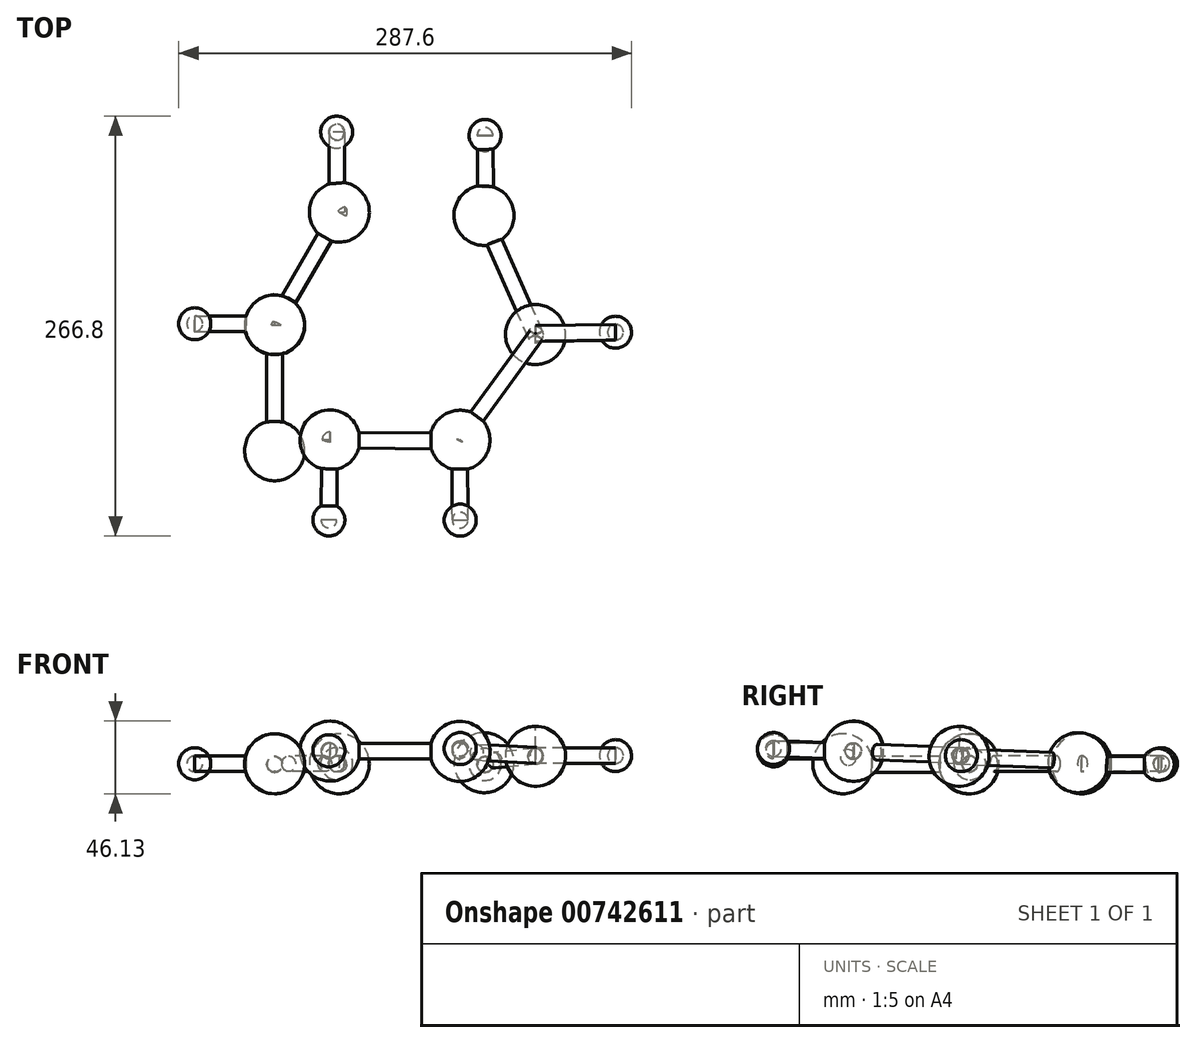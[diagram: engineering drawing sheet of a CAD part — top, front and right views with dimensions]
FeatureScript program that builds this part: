
annotation { "Feature Type Name" : "Feature", "Feature Type Description" : "" }
export const myFeature = defineFeature(function(context is Context, id is Id, definition is map)
    precondition{}
    {
        {
            var Q0;
            Q0=qCreatedBy(makeId("Front.planeOp"),FACE);
            var sketch = newSketch(context, id + "F0", { "sketchPlane" : qUnion([Q0])});
            skLineSegment(sketch, "E0", {"start": v(0, 0) * mm, "end": v(0, 38.1) * mm});
            skArc(sketch, "E1", {"start": v(0, 0) * mm, "mid": v(19.05, 19.05) * mm, "end": v(0, 38.1) * mm});
            skSolve(sketch);
        }
        {
            var Q0;
            {var subQ0=sQuery(id+"F0.wireOp",EDGE,"E0");Q0=makeQuery(id+"F0.imprint","IMPRINT",FACE,{"disambiguationData":[TD([[makeQuery(id+"F0.imprint","IMPRINT",EDGE,{"derivedFrom":subQ0}),-1.0]])]});}
            var Q1;
            Q1=sQuery(id+"F0.wireOp",EDGE,"E0");
            revolve(context, id + "F1", {"surfaceOperationType" : NewSurfaceOperationType.NEW, "entities" : qUnion([Q0]), "axis" : qUnion([Q1]), "revolveType" : RevolveType.FULL});
        }
        {
            var Q0;
            Q0=qCreatedBy(makeId("Front.planeOp"),FACE);
            cPlane(context, id + "F2", {"entities" : qUnion([Q0]), "cplaneType" : CPlaneType.OFFSET, "offset" : 16.5 * mm, "oppositeDirection" : true, "width" : 152.4 * mm, "height" : 152.4 * mm});
        }
        {
            var Q0;
            Q0=qCreatedBy(id+"F2.planeOp",FACE);
            var sketch = newSketch(context, id + "F3", { "sketchPlane" : qUnion([Q0])});
            skPoint(sketch, "E2.middle", {"position": v(0, 18.68) * mm});
            skCircle(sketch, "E3", {"center": v(0, 18.68) * mm, "radius": 4.99 * mm});
            skSolve(sketch);
        }
        {
            var Q0;
            Q0=makeQuery(id+"F3.imprint","IMPRINT",FACE,{"disambiguationData":[TD([[makeQuery(id+"F3.imprint","IMPRINT",EDGE,{"derivedFrom":sQuery(id+"F3.wireOp",EDGE,"E3")}),1.0]])]});
            extrude(context, id + "F4", {"entities" : qUnion([Q0]), "operationType" : NewBodyOperationType.ADD, "oppositeDirection" : true, "depth" : 63.5 * mm, "offsetDistance" : 25.4 * mm});
        }
        {
            var Q0;
            Q0=makeQuery(id+"F4.opExtrude","CAP_FACE",FACE,{"disambiguationData":[OSD([sQuery(id+"F3.wireOp",EDGE,"E3")])],"isStart":false});
            var sketch = newSketch(context, id + "F5", { "sketchPlane" : qUnion([Q0])});
            skArc(sketch, "E4", {"start": v(0, 0) * mm, "mid": v(18.95, 19.05) * mm, "end": v(0, 38.1) * mm});
            skLineSegment(sketch, "E5", {"start": v(0, 38.1) * mm, "end": v(0, 0) * mm});
            skSolve(sketch);
        }
        {
            var Q0;
            {var subQ0=sQuery(id+"F5.wireOp",EDGE,"E4");Q0=makeQuery(id+"F5.imprint","IMPRINT",FACE,{"disambiguationData":[TD([[makeQuery(id+"F5.imprint","IMPRINT",EDGE,{"derivedFrom":subQ0}),1.0]])]});}
            var Q1;
            Q1=sQuery(id+"F5.wireOp",EDGE,"E5");
            revolve(context, id + "F6", {"operationType" : NewBodyOperationType.ADD, "surfaceOperationType" : NewSurfaceOperationType.NEW, "entities" : qUnion([Q0]), "axis" : qUnion([Q1]), "revolveType" : RevolveType.FULL});
        }
        {
            var Q0;
            Q0=sQuery(id+"F5.wireOp",EDGE,"E5");
            var Q1;
            Q1=qCreatedBy(makeId("Right.planeOp"),FACE);
            cPlane(context, id + "F7", {"entities" : qUnion([Q0, Q1]), "cplaneType" : CPlaneType.LINE_ANGLE, "offset" : 25.4 * mm, "angle" : 120 * degree, "width" : 152.4 * mm, "height" : 152.4 * mm});
        }
        {
            var Q0;
            Q0=qCreatedBy(id+"F7.planeOp",FACE);
            var sketch = newSketch(context, id + "F8", { "sketchPlane" : qUnion([Q0])});
            skLineSegment(sketch, "E6", {"start": v(40.25, 0) * mm, "end": v(40.25, 38.1) * mm});
            skLineSegment(sketch, "E7", {"start": v(40.25, 0) * mm, "end": v(40.25, 19.05) * mm});
            skCircle(sketch, "E8", {"center": v(40.25, 19.05) * mm, "radius": 5 * mm});
            skSolve(sketch);
        }
        {
            var Q0;
            {var subQ1=sQuery(id+"F8.wireOp",EDGE,"E6");var subQ3=makeQuery(id+"F8.imprint","IMPRINT",VERTEX,{"derivedFrom":subQ1});var subQ4=makeQuery(id+"F8.imprint","IMPRINT",EDGE,{"disambiguationData":[TD([[subQ3,-1.0]])],"derivedFrom":subQ1});Q0=qUnion([makeQuery(id+"F8.imprint","IMPRINT",FACE,{"disambiguationData":[TD([[subQ4,1.0]])]}),makeQuery(id+"F8.imprint","IMPRINT",FACE,{"disambiguationData":[TD([[subQ4,-1.0]])]})]);}
            extrude(context, id + "F9", {"entities" : qUnion([Q0]), "operationType" : NewBodyOperationType.ADD, "depth" : 82.55 * mm, "offsetDistance" : 25.4 * mm});
        }
        {
            var Q0;
            Q0=makeQuery(id+"F9.opExtrude","CAP_FACE",FACE,{"disambiguationData":[OSD([sQuery(id+"F8.wireOp",EDGE,"E8")])],"isStart":false});
            var sketch = newSketch(context, id + "F10", { "sketchPlane" : qUnion([Q0])});
            skLineSegment(sketch, "E9", {"start": v(40.25, 24.04) * mm, "end": v(40.25, 14.06) * mm});
            skLineSegment(sketch, "E10", {"start": v(40.25, 14.06) * mm, "end": v(40.25, 24.04) * mm});
            skLineSegment(sketch, "E11", {"start": v(40.25, 14.06) * mm, "end": v(40.25, 19.05) * mm});
            skLineSegment(sketch, "E12", {"start": v(40.25, 19.05) * mm, "end": v(40.25, 38.1) * mm});
            skLineSegment(sketch, "E13", {"start": v(40.25, 19.05) * mm, "end": v(40.25, 0) * mm});
            skArc(sketch, "E14", {"start": v(40.25, 0) * mm, "mid": v(59.3, 19.05) * mm, "end": v(40.25, 38.1) * mm});
            skSolve(sketch);
        }
        {
            var Q0;
            {var subQ4=sQuery(id+"F10.wireOp",EDGE,"E13");Q0=makeQuery(id+"F10.imprint","IMPRINT",FACE,{"disambiguationData":[TD([[makeQuery(id+"F10.imprint","IMPRINT",EDGE,{"derivedFrom":subQ4}),1.0]])]});}
            var Q1;
            Q1=sQuery(id+"F10.wireOp",EDGE,"E11");
            revolve(context, id + "F11", {"operationType" : NewBodyOperationType.ADD, "surfaceOperationType" : NewSurfaceOperationType.NEW, "entities" : qUnion([Q0]), "axis" : qUnion([Q1]), "revolveType" : RevolveType.FULL});
        }
        {
            var Q0;
            Q0=qCreatedBy(makeId("Right.planeOp"),FACE);
            cPlane(context, id + "F12", {"entities" : qUnion([Q0]), "cplaneType" : CPlaneType.OFFSET, "offset" : 40.13 * mm, "width" : 152.4 * mm, "height" : 152.4 * mm});
        }
        {
            var Q0;
            Q0=qCreatedBy(id+"F12.planeOp",FACE);
            var sketch = newSketch(context, id + "F13", { "sketchPlane" : qUnion([Q0])});
            skLineSegment(sketch, "E15", {"start": v(137.87, 4.1) * mm, "end": v(163.67, 32.13) * mm});
            skCircle(sketch, "E16", {"center": v(150.77, 18.11) * mm, "radius": 5 * mm});
            skSolve(sketch);
        }
        {
            var Q0;
            Q0=qCreatedBy(id+"F7.planeOp",FACE);
            cPlane(context, id + "F14", {"entities" : qUnion([Q0]), "cplaneType" : CPlaneType.OFFSET, "offset" : 81.53 * mm, "width" : 152.4 * mm, "height" : 152.4 * mm});
        }
        {
            var Q0;
            Q0=sQuery(id+"F13.wireOp",EDGE,"E15");
            var Q1;
            Q1=qCreatedBy(id+"F14.planeOp",FACE);
            cPlane(context, id + "F15", {"entities" : qUnion([Q0, Q1]), "cplaneType" : CPlaneType.LINE_ANGLE, "offset" : 25.4 * mm, "angle" : 120 * degree, "width" : 152.4 * mm, "height" : 152.4 * mm});
        }
        {
            var Q0;
            Q0=sQuery(id+"F13.wireOp",EDGE,"E16");
            extrude(context, id + "F16", {"bodyType" : ToolBodyType.SURFACE, "surfaceEntities" : qUnion([Q0]), "depth" : 82.55 * mm, "offsetDistance" : 25.4 * mm});
        }
        {
            var Q0;
            Q0=qCreatedBy(id+"F15.planeOp",FACE);
            cPlane(context, id + "F17", {"entities" : qUnion([Q0]), "cplaneType" : CPlaneType.OFFSET, "offset" : 92.2 * mm, "width" : 152.4 * mm, "height" : 152.4 * mm});
        }
        {
            var Q0;
            Q0=qCreatedBy(id+"F17.planeOp",FACE);
            var sketch = newSketch(context, id + "F18", { "sketchPlane" : qUnion([Q0])});
            skLineSegment(sketch, "E17", {"start": v(162.64, 11.86) * mm, "end": v(162.64, 1.88) * mm});
            skLineSegment(sketch, "E18", {"start": v(162.64, 1.88) * mm, "end": v(162.64, 6.87) * mm});
            skLineSegment(sketch, "E19", {"start": v(162.64, 6.87) * mm, "end": v(162.64, 25.92) * mm});
            skLineSegment(sketch, "E20", {"start": v(162.64, 6.87) * mm, "end": v(162.64, -12.18) * mm});
            skArc(sketch, "E21", {"start": v(162.64, -12.18) * mm, "mid": v(181.7, 6.87) * mm, "end": v(162.64, 25.92) * mm});
            skSolve(sketch);
        }
        {
            var Q0;
            {var subQ3=sQuery(id+"F18.wireOp",EDGE,"E21");Q0=makeQuery(id+"F18.imprint","IMPRINT",FACE,{"disambiguationData":[TD([[makeQuery(id+"F18.imprint","IMPRINT",EDGE,{"derivedFrom":subQ3}),1.0]])]});}
            var Q1;
            Q1=sQuery(id+"F18.wireOp",EDGE,"E19");
            revolve(context, id + "F19", {"surfaceOperationType" : NewSurfaceOperationType.NEW, "entities" : qUnion([Q0]), "axis" : qUnion([Q1]), "revolveType" : RevolveType.FULL});
        }
        {
            var Q0;
            Q0=sQuery(id+"F18.wireOp",EDGE,"E20");
            var Q1;
            Q1=qCreatedBy(id+"F17.planeOp",FACE);
            cPlane(context, id + "F20", {"entities" : qUnion([Q0, Q1]), "cplaneType" : CPlaneType.LINE_ANGLE, "offset" : 25.4 * mm, "angle" : 120 * degree, "oppositeDirection" : true, "width" : 152.4 * mm, "height" : 152.4 * mm});
        }
        {
            var Q0;
            Q0=qCreatedBy(id+"F20.planeOp",FACE);
            var sketch = newSketch(context, id + "F21", { "sketchPlane" : qUnion([Q0])});
            skLineSegment(sketch, "E22", {"start": v(180.95, 54.99) * mm, "end": v(180.95, -1.08) * mm});
            skLineSegment(sketch, "E23", {"start": v(180.95, -1.08) * mm, "end": v(180.95, 26.96) * mm});
            skCircle(sketch, "E24", {"center": v(180.95, 26.96) * mm, "radius": 5 * mm});
            skSolve(sketch);
        }
        {
            var Q0;
            {var subQ1=sQuery(id+"F21.wireOp",EDGE,"E22");var subQ3=makeQuery(id+"F21.imprint","IMPRINT",VERTEX,{"derivedFrom":subQ1});var subQ4=makeQuery(id+"F21.imprint","IMPRINT",EDGE,{"disambiguationData":[TD([[subQ3,-1.0]])],"derivedFrom":subQ1});Q0=qUnion([makeQuery(id+"F21.imprint","IMPRINT",FACE,{"disambiguationData":[TD([[subQ4,-1.0]])]}),makeQuery(id+"F21.imprint","IMPRINT",FACE,{"disambiguationData":[TD([[subQ4,1.0]])]})]);}
            extrude(context, id + "F22", {"entities" : qUnion([Q0]), "operationType" : NewBodyOperationType.ADD, "depth" : 82.55 * mm, "offsetDistance" : 25.4 * mm});
        }
        {
            var Q0;
            Q0=makeQuery(id+"F22.opExtrude","CAP_FACE",FACE,{"disambiguationData":[OSD([sQuery(id+"F21.wireOp",EDGE,"E24")])],"isStart":false});
            var sketch = newSketch(context, id + "F23", { "sketchPlane" : qUnion([Q0])});
            skLineSegment(sketch, "E25", {"start": v(180.87, 21.97) * mm, "end": v(180.87, 31.95) * mm});
            skLineSegment(sketch, "E26", {"start": v(180.87, 31.95) * mm, "end": v(180.95, 26.96) * mm});
            skLineSegment(sketch, "E27", {"start": v(180.95, 26.96) * mm, "end": v(180.95, 7.9) * mm});
            skLineSegment(sketch, "E28", {"start": v(180.95, 26.96) * mm, "end": v(180.87, 46) * mm});
            skArc(sketch, "E29", {"start": v(180.87, 46) * mm, "mid": v(161.9, 26.91) * mm, "end": v(180.95, 7.9) * mm});
            skSolve(sketch);
        }
        {
            var Q0;
            {var subQ4=sQuery(id+"F23.wireOp",EDGE,"E29");Q0=makeQuery(id+"F23.imprint","IMPRINT",FACE,{"disambiguationData":[TD([[makeQuery(id+"F23.imprint","IMPRINT",EDGE,{"derivedFrom":subQ4}),1.0]])]});}
            var Q1;
            Q1=sQuery(id+"F23.wireOp",EDGE,"E27");
            revolve(context, id + "F24", {"surfaceOperationType" : NewSurfaceOperationType.NEW, "entities" : qUnion([Q0]), "axis" : qUnion([Q1]), "revolveType" : RevolveType.FULL});
        }
        {
            var Q0;
            Q0=qCreatedBy(id+"F20.planeOp",FACE);
            cPlane(context, id + "F25", {"entities" : qUnion([Q0]), "cplaneType" : CPlaneType.OFFSET, "offset" : 93.73 * mm, "width" : 152.4 * mm, "height" : 152.4 * mm});
        }
        {
            var Q0;
            Q0=sQuery(id+"F23.wireOp",EDGE,"E28");
            var Q1;
            Q1=qCreatedBy(id+"F25.planeOp",FACE);
            cPlane(context, id + "F26", {"entities" : qUnion([Q0, Q1]), "cplaneType" : CPlaneType.LINE_ANGLE, "offset" : 25.4 * mm, "angle" : 120 * degree, "width" : 152.4 * mm, "height" : 152.4 * mm});
        }
        {
            var Q0;
            Q0=qCreatedBy(id+"F26.planeOp",FACE);
            var sketch = newSketch(context, id + "F27", { "sketchPlane" : qUnion([Q0])});
            skLineSegment(sketch, "E30", {"start": v(91.63, 46.21) * mm, "end": v(91.63, 8.11) * mm});
            skLineSegment(sketch, "E31", {"start": v(91.63, 8.11) * mm, "end": v(91.63, 27.16) * mm});
            skCircle(sketch, "E32", {"center": v(91.63, 27.16) * mm, "radius": 5 * mm});
            skSolve(sketch);
        }
        {
            var Q0;
            {var subQ0=sQuery(id+"F27.wireOp",EDGE,"E30");var subQ1=makeQuery(id+"F27.imprint","IMPRINT",VERTEX,{"derivedFrom":subQ0});var subQ4=makeQuery(id+"F27.imprint","IMPRINT",EDGE,{"disambiguationData":[TD([[subQ1,1.0]])],"derivedFrom":subQ0});Q0=qUnion([makeQuery(id+"F27.imprint","IMPRINT",FACE,{"disambiguationData":[TD([[subQ4,1.0]])]}),makeQuery(id+"F27.imprint","IMPRINT",FACE,{"disambiguationData":[TD([[subQ4,-1.0]])]})]);}
            extrude(context, id + "F28", {"entities" : qUnion([Q0]), "depth" : 82.55 * mm, "offsetDistance" : 25.4 * mm});
        }
        {
            var Q0;
            Q0=makeQuery(id+"F28.opExtrude","CAP_FACE",FACE,{"disambiguationData":[OSD([sQuery(id+"F27.wireOp",EDGE,"E32")])],"isStart":false});
            var sketch = newSketch(context, id + "F29", { "sketchPlane" : qUnion([Q0])});
            skLineSegment(sketch, "E33", {"start": v(91.77, 32.15) * mm, "end": v(91.77, 22.17) * mm});
            skLineSegment(sketch, "E34", {"start": v(91.77, 22.17) * mm, "end": v(91.77, 27.16) * mm});
            skLineSegment(sketch, "E35", {"start": v(91.77, 27.16) * mm, "end": v(91.77, 46.21) * mm});
            skLineSegment(sketch, "E36", {"start": v(91.77, 27.16) * mm, "end": v(91.77, 8.11) * mm});
            skArc(sketch, "E37", {"start": v(91.77, 8.11) * mm, "mid": v(110.82, 27.16) * mm, "end": v(91.77, 46.21) * mm});
            skSolve(sketch);
        }
        {
            var Q0;
            {var subQ0=sQuery(id+"F29.wireOp",EDGE,"E37");Q0=makeQuery(id+"F29.imprint","IMPRINT",FACE,{"disambiguationData":[TD([[makeQuery(id+"F29.imprint","IMPRINT",EDGE,{"derivedFrom":subQ0}),1.0]])]});}
            var Q1;
            Q1=sQuery(id+"F29.wireOp",EDGE,"E35");
            revolve(context, id + "F30", {"operationType" : NewBodyOperationType.ADD, "surfaceOperationType" : NewSurfaceOperationType.NEW, "entities" : qUnion([Q0]), "axis" : qUnion([Q1]), "revolveType" : RevolveType.FULL});
        }
        {
            var Q0;
            Q0=qCreatedBy(id+"F26.planeOp",FACE);
            cPlane(context, id + "F31", {"entities" : qUnion([Q0]), "cplaneType" : CPlaneType.OFFSET, "offset" : 87.12 * mm, "width" : 152.4 * mm, "height" : 152.4 * mm});
        }
        {
            var Q0;
            Q0=sQuery(id+"F29.wireOp",EDGE,"E35");
            var Q1;
            Q1=qCreatedBy(id+"F31.planeOp",FACE);
            cPlane(context, id + "F32", {"entities" : qUnion([Q0, Q1]), "cplaneType" : CPlaneType.LINE_ANGLE, "offset" : 25.4 * mm, "angle" : 125.5 * degree, "width" : 152.4 * mm, "height" : 152.4 * mm});
        }
        {
            var Q0;
            Q0=qCreatedBy(id+"F32.planeOp",FACE);
            var sketch = newSketch(context, id + "F33", { "sketchPlane" : qUnion([Q0])});
            skLineSegment(sketch, "E38", {"start": v(-7.24, 46.11) * mm, "end": v(-7.24, 8.01) * mm});
            skLineSegment(sketch, "E39", {"start": v(-7.24, 8.01) * mm, "end": v(-7.24, 27.06) * mm});
            skCircle(sketch, "E40", {"center": v(-7.24, 27.06) * mm, "radius": 5 * mm});
            skSolve(sketch);
        }
        {
            var Q0;
            {var subQ0=sQuery(id+"F33.wireOp",EDGE,"E38");var subQ1=makeQuery(id+"F33.imprint","IMPRINT",VERTEX,{"derivedFrom":subQ0});var subQ4=makeQuery(id+"F33.imprint","IMPRINT",EDGE,{"disambiguationData":[TD([[subQ1,1.0]])],"derivedFrom":subQ0});Q0=qUnion([makeQuery(id+"F33.imprint","IMPRINT",FACE,{"disambiguationData":[TD([[subQ4,-1.0]])]}),makeQuery(id+"F33.imprint","IMPRINT",FACE,{"disambiguationData":[TD([[subQ4,1.0]])]})]);}
            extrude(context, id + "F34", {"entities" : qUnion([Q0]), "operationType" : NewBodyOperationType.ADD, "depth" : 82.55 * mm, "offsetDistance" : 25.4 * mm});
        }
        {
            var Q0;
            Q0=makeQuery(id+"F34.opExtrude","CAP_FACE",FACE,{"disambiguationData":[OSD([sQuery(id+"F33.wireOp",EDGE,"E40")])],"isStart":false});
            var sketch = newSketch(context, id + "F35", { "sketchPlane" : qUnion([Q0])});
            skLineSegment(sketch, "E41", {"start": v(-7.7, 32.03) * mm, "end": v(-7.24, 27.06) * mm});
            skLineSegment(sketch, "E42", {"start": v(-7.24, 27.06) * mm, "end": v(-7.24, 46.11) * mm});
            skLineSegment(sketch, "E43", {"start": v(-7.24, 27.06) * mm, "end": v(-7.24, 8.01) * mm});
            skArc(sketch, "E44", {"start": v(-7.24, 8.01) * mm, "mid": v(11.81, 27.06) * mm, "end": v(-7.24, 46.11) * mm});
            skSolve(sketch);
        }
        {
            var Q0;
            {var subQ0=sQuery(id+"F35.wireOp",EDGE,"E44");Q0=makeQuery(id+"F35.imprint","IMPRINT",FACE,{"disambiguationData":[TD([[makeQuery(id+"F35.imprint","IMPRINT",EDGE,{"derivedFrom":subQ0}),1.0]])]});}
            var Q1;
            Q1=sQuery(id+"F35.wireOp",EDGE,"E42");
            revolve(context, id + "F36", {"operationType" : NewBodyOperationType.ADD, "surfaceOperationType" : NewSurfaceOperationType.NEW, "entities" : qUnion([Q0]), "axis" : qUnion([Q1]), "revolveType" : RevolveType.FULL});
        }
        {
            var Q0;
            Q0=qCreatedBy(id+"F32.planeOp",FACE);
            cPlane(context, id + "F37", {"entities" : qUnion([Q0]), "cplaneType" : CPlaneType.OFFSET, "offset" : 78.49 * mm, "width" : 152.4 * mm, "height" : 152.4 * mm});
        }
        {
            var Q0;
            Q0=sQuery(id+"F35.wireOp",EDGE,"E42");
            var Q1;
            Q1=qCreatedBy(id+"F37.planeOp",FACE);
            cPlane(context, id + "F38", {"entities" : qUnion([Q0, Q1]), "cplaneType" : CPlaneType.LINE_ANGLE, "offset" : 25.4 * mm, "angle" : 120 * degree, "width" : 152.4 * mm, "height" : 152.4 * mm});
        }
        {
            var Q0;
            Q0=qCreatedBy(id+"F38.planeOp",FACE);
            var sketch = newSketch(context, id + "F39", { "sketchPlane" : qUnion([Q0])});
            skLineSegment(sketch, "E45", {"start": v(-35.26, 46.48) * mm, "end": v(-35.26, 8.38) * mm});
            skLineSegment(sketch, "E46", {"start": v(-35.26, 8.38) * mm, "end": v(-35.26, 27.43) * mm});
            skCircle(sketch, "E47", {"center": v(-35.26, 27.43) * mm, "radius": 5 * mm});
            skSolve(sketch);
        }
        {
            var Q0;
            Q0=sQuery(id+"F39.wireOp",EDGE,"E47");
            extrude(context, id + "F40", {"bodyType" : ToolBodyType.SURFACE, "surfaceEntities" : qUnion([Q0]), "depth" : 86.36 * mm, "offsetDistance" : 25.4 * mm});
        }
        {
            var Q0;
            Q0=sQuery(id+"F18.wireOp",EDGE,"E20");
            var Q1;
            Q1=qCreatedBy(id+"F17.planeOp",FACE);
            cPlane(context, id + "F41", {"entities" : qUnion([Q0, Q1]), "cplaneType" : CPlaneType.LINE_ANGLE, "offset" : 25.4 * mm, "angle" : 83.5 * degree, "width" : 152.4 * mm, "height" : 152.4 * mm});
        }
        {
            var Q0;
            Q0=qCreatedBy(id+"F41.planeOp",FACE);
            var sketch = newSketch(context, id + "F42", { "sketchPlane" : qUnion([Q0])});
            skLineSegment(sketch, "E48", {"start": v(-135.47, -0.26) * mm, "end": v(-135.47, 37.84) * mm});
            skLineSegment(sketch, "E49", {"start": v(-135.47, 37.84) * mm, "end": v(-135.47, 18.79) * mm});
            skCircle(sketch, "E50", {"center": v(-135.47, 18.79) * mm, "radius": 5 * mm});
            skSolve(sketch);
        }
        {
            var Q0;
            {var subQ1=sQuery(id+"F42.wireOp",EDGE,"E48");var subQ3=makeQuery(id+"F42.imprint","IMPRINT",VERTEX,{"derivedFrom":subQ1});var subQ4=makeQuery(id+"F42.imprint","IMPRINT",EDGE,{"disambiguationData":[TD([[subQ3,-1.0]])],"derivedFrom":subQ1});Q0=qUnion([makeQuery(id+"F42.imprint","IMPRINT",FACE,{"disambiguationData":[TD([[subQ4,1.0]])]}),makeQuery(id+"F42.imprint","IMPRINT",FACE,{"disambiguationData":[TD([[subQ4,-1.0]])]})]);}
            extrude(context, id + "F43", {"entities" : qUnion([Q0]), "operationType" : NewBodyOperationType.ADD, "depth" : 50.8 * mm, "offsetDistance" : 25.4 * mm});
        }
        {
            var Q0;
            Q0=makeQuery(id+"F43.opExtrude","CAP_FACE",FACE,{"disambiguationData":[OSD([sQuery(id+"F42.wireOp",EDGE,"E50")])],"isStart":false});
            var sketch = newSketch(context, id + "F44", { "sketchPlane" : qUnion([Q0])});
            skLineSegment(sketch, "E51", {"start": v(-135.47, 13.8) * mm, "end": v(-135.47, 23.78) * mm});
            skLineSegment(sketch, "E52", {"start": v(-135.47, 23.78) * mm, "end": v(-135.47, 18.79) * mm});
            skLineSegment(sketch, "E53", {"start": v(-135.47, 18.79) * mm, "end": v(-135.47, 28.95) * mm});
            skLineSegment(sketch, "E54", {"start": v(-135.47, 18.79) * mm, "end": v(-135.47, 8.63) * mm});
            skArc(sketch, "E55", {"start": v(-135.47, 8.63) * mm, "mid": v(-125.3, 18.79) * mm, "end": v(-135.47, 28.95) * mm});
            skSolve(sketch);
        }
        {
            var Q0;
            {var subQ0=sQuery(id+"F44.wireOp",EDGE,"E55");Q0=makeQuery(id+"F44.imprint","IMPRINT",FACE,{"disambiguationData":[TD([[makeQuery(id+"F44.imprint","IMPRINT",EDGE,{"derivedFrom":subQ0}),1.0]])]});}
            var Q1;
            Q1=sQuery(id+"F44.wireOp",EDGE,"E53");
            revolve(context, id + "F45", {"operationType" : NewBodyOperationType.ADD, "surfaceOperationType" : NewSurfaceOperationType.NEW, "entities" : qUnion([Q0]), "axis" : qUnion([Q1]), "revolveType" : RevolveType.FULL});
        }
        {
            var Q0;
            Q0=sQuery(id+"F10.wireOp",EDGE,"E12");
            var Q1;
            Q1=qCreatedBy(id+"F14.planeOp",FACE);
            cPlane(context, id + "F46", {"entities" : qUnion([Q0, Q1]), "cplaneType" : CPlaneType.LINE_ANGLE, "offset" : 25.4 * mm, "angle" : 30 * degree, "width" : 152.4 * mm, "height" : 152.4 * mm});
        }
        {
            var Q0;
            Q0=qCreatedBy(id+"F46.planeOp",FACE);
            var sketch = newSketch(context, id + "F47", { "sketchPlane" : qUnion([Q0])});
            skLineSegment(sketch, "E56", {"start": v(39.55, 0) * mm, "end": v(39.55, 38.1) * mm});
            skLineSegment(sketch, "E57", {"start": v(39.55, 38.1) * mm, "end": v(39.55, 19.05) * mm});
            skCircle(sketch, "E58", {"center": v(39.55, 19.05) * mm, "radius": 5 * mm});
            skSolve(sketch);
        }
        {
            var Q0;
            {var subQ1=sQuery(id+"F47.wireOp",EDGE,"E56");var subQ3=makeQuery(id+"F47.imprint","IMPRINT",VERTEX,{"derivedFrom":subQ1});var subQ4=makeQuery(id+"F47.imprint","IMPRINT",EDGE,{"disambiguationData":[TD([[subQ3,-1.0]])],"derivedFrom":subQ1});Q0=qUnion([makeQuery(id+"F47.imprint","IMPRINT",FACE,{"disambiguationData":[TD([[subQ4,1.0]])]}),makeQuery(id+"F47.imprint","IMPRINT",FACE,{"disambiguationData":[TD([[subQ4,-1.0]])]})]);}
            extrude(context, id + "F48", {"entities" : qUnion([Q0]), "operationType" : NewBodyOperationType.ADD, "oppositeDirection" : true, "depth" : 50.8 * mm, "offsetDistance" : 25.4 * mm});
        }
        {
            var Q0;
            Q0=makeQuery(id+"F48.opExtrude","CAP_FACE",FACE,{"disambiguationData":[OSD([sQuery(id+"F47.wireOp",EDGE,"E58")])],"isStart":false});
            var sketch = newSketch(context, id + "F49", { "sketchPlane" : qUnion([Q0])});
            skLineSegment(sketch, "E59", {"start": v(-39.4, 14.06) * mm, "end": v(-39.4, 24.04) * mm});
            skLineSegment(sketch, "E60", {"start": v(-39.4, 24.04) * mm, "end": v(-39.4, 19.05) * mm});
            skLineSegment(sketch, "E61", {"start": v(-39.4, 19.05) * mm, "end": v(-39.4, 8.89) * mm});
            skLineSegment(sketch, "E62", {"start": v(-39.4, 19.05) * mm, "end": v(-39.4, 29.21) * mm});
            skArc(sketch, "E63", {"start": v(-39.4, 29.21) * mm, "mid": v(-49.55, 19.05) * mm, "end": v(-39.4, 8.89) * mm});
            skSolve(sketch);
        }
        {
            var Q0;
            {var subQ0=sQuery(id+"F49.wireOp",EDGE,"E63");Q0=makeQuery(id+"F49.imprint","IMPRINT",FACE,{"disambiguationData":[TD([[makeQuery(id+"F49.imprint","IMPRINT",EDGE,{"derivedFrom":subQ0}),1.0]])]});}
            var Q1;
            Q1=sQuery(id+"F49.wireOp",EDGE,"E61");
            revolve(context, id + "F50", {"surfaceOperationType" : NewSurfaceOperationType.NEW, "entities" : qUnion([Q0]), "axis" : qUnion([Q1]), "revolveType" : RevolveType.FULL});
        }
        {
            var Q0;
            Q0=sQuery(id+"F5.wireOp",EDGE,"E5");
            var Q1;
            Q1=qCreatedBy(id+"F7.planeOp",FACE);
            cPlane(context, id + "F51", {"entities" : qUnion([Q0, Q1]), "cplaneType" : CPlaneType.LINE_ANGLE, "offset" : 25.4 * mm, "angle" : 60 * degree, "width" : 152.4 * mm, "height" : 152.4 * mm});
        }
        {
            var Q0;
            Q0=qCreatedBy(id+"F51.planeOp",FACE);
            var sketch = newSketch(context, id + "F52", { "sketchPlane" : qUnion([Q0])});
            skLineSegment(sketch, "E64", {"start": v(-80.7, 38.1) * mm, "end": v(-80.7, 0) * mm});
            skLineSegment(sketch, "E65", {"start": v(-80.7, 0) * mm, "end": v(-80.7, 19.05) * mm});
            skCircle(sketch, "E66", {"center": v(-80.7, 19.05) * mm, "radius": 5 * mm});
            skSolve(sketch);
        }
        {
            var Q0;
            {var subQ1=sQuery(id+"F52.wireOp",EDGE,"E64");var subQ3=makeQuery(id+"F52.imprint","IMPRINT",VERTEX,{"derivedFrom":subQ1});var subQ4=makeQuery(id+"F52.imprint","IMPRINT",EDGE,{"disambiguationData":[TD([[subQ3,-1.0]])],"derivedFrom":subQ1});Q0=qUnion([makeQuery(id+"F52.imprint","IMPRINT",FACE,{"disambiguationData":[TD([[subQ4,-1.0]])]}),makeQuery(id+"F52.imprint","IMPRINT",FACE,{"disambiguationData":[TD([[subQ4,1.0]])]})]);}
            extrude(context, id + "F53", {"entities" : qUnion([Q0]), "operationType" : NewBodyOperationType.ADD, "depth" : 50.8 * mm, "offsetDistance" : 25.4 * mm});
        }
        {
            var Q0;
            Q0=makeQuery(id+"F53.opExtrude","CAP_FACE",FACE,{"disambiguationData":[OSD([sQuery(id+"F52.wireOp",EDGE,"E66")])],"isStart":false});
            var sketch = newSketch(context, id + "F54", { "sketchPlane" : qUnion([Q0])});
            skLineSegment(sketch, "E67", {"start": v(-80.7, 19.05) * mm, "end": v(-80.7, 29.21) * mm});
            skLineSegment(sketch, "E68", {"start": v(-80.7, 19.05) * mm, "end": v(-80.7, 8.89) * mm});
            skArc(sketch, "E69", {"start": v(-80.7, 8.89) * mm, "mid": v(-70.53, 19.05) * mm, "end": v(-80.7, 29.21) * mm});
            skSolve(sketch);
        }
        {
            var Q0;
            {var subQ0=sQuery(id+"F54.wireOp",EDGE,"E69");Q0=makeQuery(id+"F54.imprint","IMPRINT",FACE,{"disambiguationData":[TD([[makeQuery(id+"F54.imprint","IMPRINT",EDGE,{"derivedFrom":subQ0}),1.0]])]});}
            var Q1;
            Q1=sQuery(id+"F54.wireOp",EDGE,"E67");
            revolve(context, id + "F55", {"surfaceOperationType" : NewSurfaceOperationType.NEW, "entities" : qUnion([Q0]), "axis" : qUnion([Q1]), "revolveType" : RevolveType.FULL});
        }
        {
            var Q0;
            Q0=sQuery(id+"F23.wireOp",EDGE,"E27");
            var Q1;
            Q1=qCreatedBy(id+"F25.planeOp",FACE);
            cPlane(context, id + "F56", {"entities" : qUnion([Q0, Q1]), "cplaneType" : CPlaneType.LINE_ANGLE, "offset" : 25.4 * mm, "angle" : 67 * degree, "oppositeDirection" : true, "width" : 152.4 * mm, "height" : 152.4 * mm});
        }
        {
            var Q0;
            Q0=qCreatedBy(id+"F56.planeOp",FACE);
            var sketch = newSketch(context, id + "F57", { "sketchPlane" : qUnion([Q0])});
            skLineSegment(sketch, "E70", {"start": v(-71.82, 5.32) * mm, "end": v(-71.82, 43.42) * mm});
            skLineSegment(sketch, "E71", {"start": v(-71.82, 43.42) * mm, "end": v(-71.82, 24.37) * mm});
            skCircle(sketch, "E72", {"center": v(-71.82, 24.37) * mm, "radius": 5 * mm});
            skSolve(sketch);
        }
        {
            var Q0;
            {var subQ0=sQuery(id+"F57.wireOp",EDGE,"E70");var subQ1=makeQuery(id+"F57.imprint","IMPRINT",VERTEX,{"derivedFrom":subQ0});var subQ4=makeQuery(id+"F57.imprint","IMPRINT",EDGE,{"disambiguationData":[TD([[subQ1,-1.0]])],"derivedFrom":subQ0});Q0=qUnion([makeQuery(id+"F57.imprint","IMPRINT",FACE,{"disambiguationData":[TD([[subQ4,1.0]])]}),makeQuery(id+"F57.imprint","IMPRINT",FACE,{"disambiguationData":[TD([[subQ4,-1.0]])]})]);}
            extrude(context, id + "F58", {"entities" : qUnion([Q0]), "oppositeDirection" : true, "depth" : 50.8 * mm, "offsetDistance" : 25.4 * mm});
        }
        {
            var Q0;
            Q0=makeQuery(id+"F58.opExtrude","CAP_FACE",FACE,{"disambiguationData":[OSD([sQuery(id+"F57.wireOp",EDGE,"E72")])],"isStart":false});
            var sketch = newSketch(context, id + "F59", { "sketchPlane" : qUnion([Q0])});
            skLineSegment(sketch, "E73", {"start": v(71.82, 24.37) * mm, "end": v(61.66, 24.37) * mm});
            skLineSegment(sketch, "E74", {"start": v(71.82, 24.37) * mm, "end": v(81.98, 24.37) * mm});
            skArc(sketch, "E75", {"start": v(81.98, 24.37) * mm, "mid": v(71.82, 34.53) * mm, "end": v(61.66, 24.37) * mm});
            skSolve(sketch);
        }
        {
            var Q0;
            {var subQ0=sQuery(id+"F59.wireOp",EDGE,"E75");Q0=makeQuery(id+"F59.imprint","IMPRINT",FACE,{"disambiguationData":[TD([[makeQuery(id+"F59.imprint","IMPRINT",EDGE,{"derivedFrom":subQ0}),1.0]])]});}
            var Q1;
            Q1=sQuery(id+"F59.wireOp",EDGE,"E73");
            revolve(context, id + "F60", {"surfaceOperationType" : NewSurfaceOperationType.NEW, "entities" : qUnion([Q0]), "axis" : qUnion([Q1]), "revolveType" : RevolveType.FULL});
        }
        {
            var Q0;
            Q0=sQuery(id+"F29.wireOp",EDGE,"E36");
            var Q1;
            Q1=qCreatedBy(id+"F31.planeOp",FACE);
            cPlane(context, id + "F61", {"entities" : qUnion([Q0, Q1]), "cplaneType" : CPlaneType.LINE_ANGLE, "offset" : 25.4 * mm, "angle" : 36.55 * degree, "oppositeDirection" : true, "width" : 152.4 * mm, "height" : 152.4 * mm});
        }
        {
            var Q0;
            Q0=qCreatedBy(id+"F61.planeOp",FACE);
            var sketch = newSketch(context, id + "F62", { "sketchPlane" : qUnion([Q0])});
            skLineSegment(sketch, "E76", {"start": v(-117.45, 46.08) * mm, "end": v(-117.45, 7.98) * mm});
            skLineSegment(sketch, "E77", {"start": v(-117.45, 7.98) * mm, "end": v(-117.45, 27.03) * mm});
            skCircle(sketch, "E78", {"center": v(-117.45, 27.03) * mm, "radius": 5 * mm});
            skSolve(sketch);
        }
        {
            var Q0;
            {var subQ1=sQuery(id+"F62.wireOp",EDGE,"E76");var subQ3=makeQuery(id+"F62.imprint","IMPRINT",VERTEX,{"derivedFrom":subQ1});var subQ4=makeQuery(id+"F62.imprint","IMPRINT",EDGE,{"disambiguationData":[TD([[subQ3,-1.0]])],"derivedFrom":subQ1});Q0=qUnion([makeQuery(id+"F62.imprint","IMPRINT",FACE,{"disambiguationData":[TD([[subQ4,-1.0]])]}),makeQuery(id+"F62.imprint","IMPRINT",FACE,{"disambiguationData":[TD([[subQ4,1.0]])]})]);}
            extrude(context, id + "F63", {"entities" : qUnion([Q0]), "operationType" : NewBodyOperationType.ADD, "oppositeDirection" : true, "depth" : 50.8 * mm, "offsetDistance" : 25.4 * mm});
        }
        {
            var Q0;
            Q0=makeQuery(id+"F63.opExtrude","CAP_FACE",FACE,{"disambiguationData":[OSD([sQuery(id+"F62.wireOp",EDGE,"E78")])],"isStart":false});
            var sketch = newSketch(context, id + "F64", { "sketchPlane" : qUnion([Q0])});
            skLineSegment(sketch, "E79", {"start": v(117.45, 27.03) * mm, "end": v(117.45, 37.2) * mm});
            skLineSegment(sketch, "E80", {"start": v(117.45, 27.03) * mm, "end": v(117.45, 16.87) * mm});
            skArc(sketch, "E81", {"start": v(117.45, 16.87) * mm, "mid": v(127.61, 27.03) * mm, "end": v(117.45, 37.2) * mm});
            skSolve(sketch);
        }
        {
            var Q0;
            {var subQ0=sQuery(id+"F64.wireOp",EDGE,"E81");Q0=makeQuery(id+"F64.imprint","IMPRINT",FACE,{"disambiguationData":[TD([[makeQuery(id+"F64.imprint","IMPRINT",EDGE,{"derivedFrom":subQ0}),1.0]])]});}
            var Q1;
            Q1=sQuery(id+"F64.wireOp",EDGE,"E80");
            revolve(context, id + "F65", {"surfaceOperationType" : NewSurfaceOperationType.NEW, "entities" : qUnion([Q0]), "axis" : qUnion([Q1]), "revolveType" : RevolveType.FULL});
        }
        {
            var Q0;
            Q0=sQuery(id+"F35.wireOp",EDGE,"E42");
            var Q1;
            Q1=qCreatedBy(id+"F38.planeOp",FACE);
            cPlane(context, id + "F66", {"entities" : qUnion([Q0, Q1]), "cplaneType" : CPlaneType.LINE_ANGLE, "offset" : 25.4 * mm, "angle" : 30 * degree, "oppositeDirection" : true, "width" : 152.4 * mm, "height" : 152.4 * mm});
        }
        {
            var Q0;
            Q0=qCreatedBy(id+"F66.planeOp",FACE);
            var sketch = newSketch(context, id + "F67", { "sketchPlane" : qUnion([Q0])});
            skLineSegment(sketch, "E82", {"start": v(34.89, 46.34) * mm, "end": v(34.89, 8.24) * mm});
            skLineSegment(sketch, "E83", {"start": v(34.89, 46.34) * mm, "end": v(34.89, 27.3) * mm});
            skCircle(sketch, "E84", {"center": v(34.89, 27.3) * mm, "radius": 5 * mm});
            skSolve(sketch);
        }
        {
            var Q0;
            {var subQ0=sQuery(id+"F67.wireOp",EDGE,"E82");var subQ1=makeQuery(id+"F67.imprint","IMPRINT",VERTEX,{"derivedFrom":subQ0});var subQ4=makeQuery(id+"F67.imprint","IMPRINT",EDGE,{"disambiguationData":[TD([[subQ1,1.0]])],"derivedFrom":subQ0});Q0=qUnion([makeQuery(id+"F67.imprint","IMPRINT",FACE,{"disambiguationData":[TD([[subQ4,-1.0]])]}),makeQuery(id+"F67.imprint","IMPRINT",FACE,{"disambiguationData":[TD([[subQ4,1.0]])]})]);}
            extrude(context, id + "F68", {"entities" : qUnion([Q0]), "operationType" : NewBodyOperationType.ADD, "depth" : 50.8 * mm, "offsetDistance" : 25.4 * mm});
        }
        {
            var Q0;
            Q0=makeQuery(id+"F68.opExtrude","CAP_FACE",FACE,{"disambiguationData":[OSD([sQuery(id+"F67.wireOp",EDGE,"E84")])],"isStart":false});
            var sketch = newSketch(context, id + "F69", { "sketchPlane" : qUnion([Q0])});
            skLineSegment(sketch, "E85", {"start": v(34.89, 27.3) * mm, "end": v(34.89, 17.13) * mm});
            skLineSegment(sketch, "E86", {"start": v(34.89, 27.3) * mm, "end": v(34.89, 37.45) * mm});
            skArc(sketch, "E87", {"start": v(34.89, 37.45) * mm, "mid": v(24.73, 27.3) * mm, "end": v(34.89, 17.13) * mm});
            skSolve(sketch);
        }
        {
            var Q0;
            {var subQ0=sQuery(id+"F69.wireOp",EDGE,"E87");Q0=makeQuery(id+"F69.imprint","IMPRINT",FACE,{"disambiguationData":[TD([[makeQuery(id+"F69.imprint","IMPRINT",EDGE,{"derivedFrom":subQ0}),1.0]])]});}
            var Q1;
            Q1=sQuery(id+"F69.wireOp",EDGE,"E86");
            revolve(context, id + "F70", {"operationType" : NewBodyOperationType.ADD, "surfaceOperationType" : NewSurfaceOperationType.NEW, "entities" : qUnion([Q0]), "axis" : qUnion([Q1]), "revolveType" : RevolveType.FULL});
        }
    });
